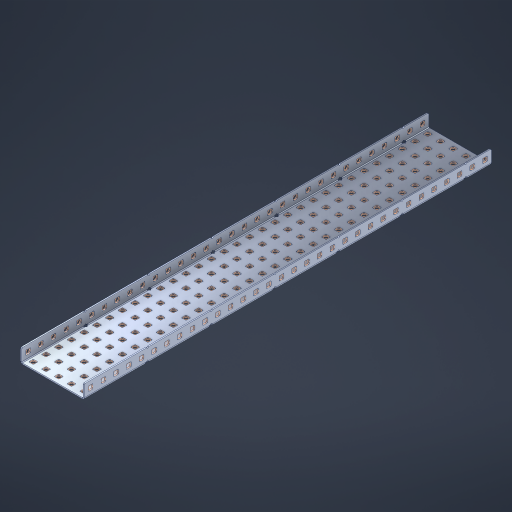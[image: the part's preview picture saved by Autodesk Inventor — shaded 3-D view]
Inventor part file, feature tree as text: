
AUTODESK INVENTOR PART (.ipt)
format: ipt  version: 2023 (Build 270158000, 158)  size: 2,352,640 bytes
history: native  units: in
note: dims shown in document units (in); Inventor stores cm internally (conversion verified against a paired STEP export)
features: other x229, extrude x223, sheet_metal_op x10, sketch x8, mirror x1, pattern_linear x1, chamfer x1
ambient origin geometry x8: Origin, YZ Plane, XZ Plane, XY Plane, X Axis, Y Axis, Z Axis, Center Point
bodies: Solid1 (feature_tree), Body (feature_tree)
feature tree (473):
  other  "Flange Pattern Plane"
  sheet_metal_op  "Flange Pattern"
  sheet_metal_op  "Body Pattern"
  other  "Arc Length"
  mirror  "Notch Mirror"
  pattern_linear  "Notch Pattern"  Spacing1=0.1875in  [1 undecoded]
  chamfer  "End Chamfer"
  extrude  "Half Cut"  Depth=0.0469in
  sketch  "Sketch1"  dims[d0=2.5in]
  other  "Plate1"
  sketch  "Sketch2"  dims[d1=16.0in]
  other  "Plate2"
  sheet_metal_op  "Bend1"
  sheet_metal_op  "Corner1"
  sketch  "Sketch3"  dims[d2=0.0469in]
  other  "Flange Pattern Sketch"
  sketch  "Sketch7"  dims[d3=0.0469in]
  other  "Srf1"
  other  "Srf2"
  sketch  "Sketch8"  dims[d4=0.0234in]
  sketch  "Sketch9"  dims[d5=0.0938in]
  other  "Srf91"
  sheet_metal_op  "Body Pattern Sketch"
  other  "Srf92"
  sketch  "Sketch13"  dims[d6=0.0469in]
  sketch  "Sketch14"  dims[d7=0.5in d8=90.0deg d9=0.0312in d10=0.1875in d11=0.0469in d12=0.0469in d16=0.182in d17=0.02in d18=0.0469in d19=0.0in d20=0.25in d21=0.25in d46=0.172in d47=1.0in d48=0.0in d49=0.182in d50=0.02in d51=0.25in d52=0.25in d53=0.0469in d54=0.0in d55=0.172in d56=1.0in d57=0.0in d60=12.5984in d62=0.5in d63=1.9685in d65=0.5in d85=0.1227in d86=0.1659in d88=0.04in d89=0.0469in d90=0.0in d91=0.04in d92=0.0491in d95=2.5in d96=0.04in d97=0.25in d98=45.0deg d101=0.0in d102=2.497in d131=2.5in d132=12.5984in d134=0.5in d139=0.5in]
  other  "Srf856"
  other  "Srf1310"
  other  "Srf1311"
  other  "Srf1312"
  other  "Srf1376"
  other  "Srf1377"
  other  "Srf1728"
  other  "Srf1755"
  other  "Srf1878"
  other  "Srf1879"
  other  "Srf1880"
  other  "Srf1881"
  other  "Srf1882"
  other  "Srf1883"
  other  "Srf1884"
  other  "Srf1885"
  other  "Srf1886"
  other  "Srf1887"
  other  "Srf1888"
  other  "Srf1889"
  other  "Srf1890"
  other  "Srf1891"
  other  "Srf1892"
  other  "Srf1893"
  other  "Srf1894"
  other  "Srf1895"
  other  "Srf1896"
  other  "Srf1897"
  other  "Srf1898"
  other  "Srf1899"
  other  "Srf1900"
  other  "Srf1901"
  other  "Srf1902"
  other  "Srf1903"
  other  "Srf1904"
  other  "Srf1905"
  other  "Srf1906"
  other  "Srf1942"
  other  "Srf1943"
  other  "Srf1944"
  other  "Srf1945"
  other  "Srf1946"
  other  "Srf1947"
  other  "Srf1948"
  other  "Srf1949"
  other  "Srf1950"
  other  "Srf1951"
  other  "Srf1952"
  other  "Srf1953"
  other  "Srf1954"
  other  "Srf1955"
  other  "Srf1956"
  other  "Srf1957"
  other  "Srf1958"
  other  "Srf1959"
  other  "Srf1960"
  other  "Srf1961"
  other  "Srf1962"
  other  "Srf1963"
  other  "Srf1964"
  other  "Srf1965"
  other  "Srf1966"
  other  "Srf1967"
  other  "Srf1968"
  other  "Srf1969"
  other  "Srf1970"
  other  "Srf2111"
  other  "Srf2112"
  other  "Srf2113"
  other  "Srf2114"
  other  "Srf2115"
  other  "Srf2116"
  other  "Srf2117"
  other  "Srf2118"
  other  "Srf2119"
  other  "Srf2120"
  other  "Srf2121"
  other  "Srf2122"
  other  "Srf2123"
  other  "Srf2124"
  other  "Srf2125"
  other  "Srf2126"
  other  "Srf2127"
  other  "Srf2128"
  other  "Srf2129"
  other  "Srf2130"
  other  "Srf2131"
  other  "Srf2132"
  other  "Srf2133"
  other  "Srf2134"
  other  "Srf2135"
  other  "Srf2136"
  other  "Srf2137"
  other  "Srf2138"
  other  "Srf2139"
  other  "Srf2146"
  other  "Srf2147"
  other  "Srf2148"
  other  "Srf2149"
  other  "Srf2150"
  other  "Srf2151"
  other  "Srf2152"
  other  "Srf2153"
  other  "Srf2154"
  other  "Srf2155"
  other  "Srf2156"
  other  "Srf2157"
  other  "Srf2158"
  other  "Srf2159"
  other  "Srf2160"
  other  "Srf2161"
  other  "Srf2162"
  other  "Srf2163"
  other  "Srf2164"
  other  "Srf2165"
  other  "Srf2166"
  other  "Srf2167"
  other  "Srf2168"
  other  "Srf2169"
  other  "Srf2170"
  other  "Srf2171"
  other  "Srf2172"
  other  "Srf2173"
  other  "Srf2174"
  other  "Srf2175"
  other  "Srf2176"
  other  "Srf2177"
  other  "Srf2178"
  other  "Srf2179"
  other  "Srf2180"
  other  "Srf2181"
  other  "Srf2182"
  other  "Srf2183"
  other  "Srf2184"
  other  "Srf2185"
  other  "Srf2186"
  other  "Srf2187"
  other  "Srf2188"
  other  "Srf2189"
  other  "Srf2190"
  other  "Srf2191"
  other  "Srf2192"
  other  "Srf2193"
  other  "Srf2194"
  other  "Srf2195"
  other  "Srf2196"
  other  "Srf2197"
  other  "Srf2198"
  other  "Srf2199"
  other  "Srf2200"
  other  "Srf2201"
  other  "Srf2202"
  other  "Srf2203"
  other  "Srf2204"
  other  "Srf2205"
  other  "Srf2206"
  other  "Srf2207"
  other  "Srf2208"
  other  "Srf2209"
  other  "Srf2210"
  other  "Srf2211"
  other  "Srf2212"
  other  "Srf2213"
  other  "Srf2214"
  other  "Srf2215"
  other  "Srf2216"
  other  "Srf2217"
  other  "Srf2218"
  other  "Srf2219"
  other  "Srf2220"
  other  "Srf2221"
  other  "Srf2222"
  other  "Srf2223"
  other  "Srf2224"
  other  "Srf2225"
  other  "Srf2226"
  other  "Srf2227"
  other  "Srf2228"
  other  "Srf2229"
  other  "Srf2230"
  other  "Srf2231"
  other  "Srf2232"
  other  "Srf2233"
  other  "Srf2234"
  other  "Srf2235"
  other  "Srf2236"
  other  "Srf2237"
  other  "Srf2238"
  other  "Srf2239"
  other  "Srf2240"
  other  "Srf2241"
  other  "Srf2242"
  other  "Srf2243"
  other  "Srf2244"
  other  "Srf2245"
  other  "Srf2246"
  other  "Srf2247"
  other  "Srf2248"
  other  "Srf2249"
  other  "Srf2250"
  other  "Srf2251"
  other  "Srf2252"
  other  "Srf2253"
  other  "Srf2254"
  other  "Srf2255"
  other  "Srf2256"
  other  "Srf2257"
  other  "Srf2258"
  other  "Srf2259"
  other  "Srf2260"
  other  "Srf2261"
  other  "Srf2262"
  other  "Srf2263"
  other  "Srf2264"
  other  "Srf2265"
  other  "Srf2266"
  other  "Srf2267"
  other  "Srf2268"
  other  "Srf2269"
  other  "Srf2270"
  sheet_metal_op  "Flange Stamp"
  sheet_metal_op  "Flange Circle"
  sheet_metal_op  "Body Stamp"
  sheet_metal_op  "Body Circle"
  sheet_metal_op  "Notch"
  extrude  "ExtrusionSrf2"  Depth=0.0469in
  extrude  "ExtrusionSrf92"  Depth=2.5in
  extrude  "ExtrusionSrf856"  Depth=0.02in
  extrude  "ExtrusionSrf1310"  Depth=0.0469in
  extrude  "ExtrusionSrf1311"  TaperAngle=0.0deg  [1 undecoded]
  extrude  "ExtrusionSrf1312"  Depth=0.25in
  extrude  "ExtrusionSrf1376"  Depth=0.25in
  extrude  "ExtrusionSrf1377"  Depth=2.5in
  extrude  "ExtrusionSrf1728"  Depth=2.5in TaperAngle=0.0deg
  extrude  "ExtrusionSrf1755"  Depth=2.5in
  extrude  "ExtrusionSrf1878"  Depth=0.02in
  extrude  "ExtrusionSrf1879"  Depth=0.25in
  extrude  "ExtrusionSrf1880"  Depth=0.25in
  extrude  "ExtrusionSrf1881"  Depth=0.0469in
  extrude  "ExtrusionSrf1882"  TaperAngle=0.0deg  [1 undecoded]
  extrude  "ExtrusionSrf1883"  Depth=2.5in
  extrude  "ExtrusionSrf1884"  Depth=2.5in TaperAngle=0.0deg
  extrude  "ExtrusionSrf1885"  Depth=2.5in
  extrude  "ExtrusionSrf1886"  Depth=2.5in
  extrude  "ExtrusionSrf1887"  Depth=2.5in
  extrude  "ExtrusionSrf1888"  Depth=2.5in
  extrude  "ExtrusionSrf1889"  Depth=2.5in
  extrude  "ExtrusionSrf1890"  Depth=0.0469in
  extrude  "ExtrusionSrf1891"  TaperAngle=0.0deg  [1 undecoded]
  extrude  "ExtrusionSrf1892"  Depth=2.5in
  extrude  "ExtrusionSrf1893"  Depth=2.5in
  extrude  "ExtrusionSrf1894"  Depth=2.5in
  extrude  "ExtrusionSrf1895"  Depth=0.25in TaperAngle=45.0deg
  extrude  "ExtrusionSrf1896"  TaperAngle=0.0deg  [1 undecoded]
  extrude  "ExtrusionSrf1897"  Depth=2.5in
  extrude  "ExtrusionSrf1898"  Depth=2.5in
  extrude  "ExtrusionSrf1899"  Depth=2.5in
  extrude  "ExtrusionSrf1900"  Depth=2.5in
  extrude  "ExtrusionSrf1901"  Depth=2.5in
  extrude  "ExtrusionSrf1902"  [1 undecoded]
  extrude  "ExtrusionSrf1903"  [1 undecoded]
  extrude  "ExtrusionSrf1904"  [1 undecoded]
  extrude  "ExtrusionSrf1905"  [1 undecoded]
  extrude  "ExtrusionSrf1906"  [1 undecoded]
  extrude  "ExtrusionSrf1942"  [1 undecoded]
  extrude  "ExtrusionSrf1943"  [1 undecoded]
  extrude  "ExtrusionSrf1944"  [1 undecoded]
  extrude  "ExtrusionSrf1945"  [1 undecoded]
  extrude  "ExtrusionSrf1946"  [1 undecoded]
  extrude  "ExtrusionSrf1947"  [1 undecoded]
  extrude  "ExtrusionSrf1948"  [1 undecoded]
  extrude  "ExtrusionSrf1949"  [1 undecoded]
  extrude  "ExtrusionSrf1950"  [1 undecoded]
  extrude  "ExtrusionSrf1951"  [1 undecoded]
  extrude  "ExtrusionSrf1952"  [1 undecoded]
  extrude  "ExtrusionSrf1953"  [1 undecoded]
  extrude  "ExtrusionSrf1954"  [1 undecoded]
  extrude  "ExtrusionSrf1955"  [1 undecoded]
  extrude  "ExtrusionSrf1956"  [1 undecoded]
  extrude  "ExtrusionSrf1957"  [1 undecoded]
  extrude  "ExtrusionSrf1958"  [1 undecoded]
  extrude  "ExtrusionSrf1959"  [1 undecoded]
  extrude  "ExtrusionSrf1960"  [1 undecoded]
  extrude  "ExtrusionSrf1961"  [1 undecoded]
  extrude  "ExtrusionSrf1962"  [1 undecoded]
  extrude  "ExtrusionSrf1963"  [1 undecoded]
  extrude  "ExtrusionSrf1964"  [1 undecoded]
  extrude  "ExtrusionSrf1965"  [1 undecoded]
  extrude  "ExtrusionSrf1966"  [1 undecoded]
  extrude  "ExtrusionSrf1967"  [1 undecoded]
  extrude  "ExtrusionSrf1968"  [1 undecoded]
  extrude  "ExtrusionSrf1969"  [1 undecoded]
  extrude  "ExtrusionSrf1970"  [1 undecoded]
  extrude  "ExtrusionSrf2111"  [1 undecoded]
  extrude  "ExtrusionSrf2112"  [1 undecoded]
  extrude  "ExtrusionSrf2113"  [1 undecoded]
  extrude  "ExtrusionSrf2114"  [1 undecoded]
  extrude  "ExtrusionSrf2115"  [1 undecoded]
  extrude  "ExtrusionSrf2116"  [1 undecoded]
  extrude  "ExtrusionSrf2117"  [1 undecoded]
  extrude  "ExtrusionSrf2118"  [1 undecoded]
  extrude  "ExtrusionSrf2119"  [1 undecoded]
  extrude  "ExtrusionSrf2120"  [1 undecoded]
  extrude  "ExtrusionSrf2121"  [1 undecoded]
  extrude  "ExtrusionSrf2122"  [1 undecoded]
  extrude  "ExtrusionSrf2123"  [1 undecoded]
  extrude  "ExtrusionSrf2124"  [1 undecoded]
  extrude  "ExtrusionSrf2125"  [1 undecoded]
  extrude  "ExtrusionSrf2126"  [1 undecoded]
  extrude  "ExtrusionSrf2127"  [1 undecoded]
  extrude  "ExtrusionSrf2128"  [1 undecoded]
  extrude  "ExtrusionSrf2129"  [1 undecoded]
  extrude  "ExtrusionSrf2130"  [1 undecoded]
  extrude  "ExtrusionSrf2131"  [1 undecoded]
  extrude  "ExtrusionSrf2132"  [1 undecoded]
  extrude  "ExtrusionSrf2133"  [1 undecoded]
  extrude  "ExtrusionSrf2134"  [1 undecoded]
  extrude  "ExtrusionSrf2135"  [1 undecoded]
  extrude  "ExtrusionSrf2136"  [1 undecoded]
  extrude  "ExtrusionSrf2137"  [1 undecoded]
  extrude  "ExtrusionSrf2138"  [1 undecoded]
  extrude  "ExtrusionSrf2139"  [1 undecoded]
  extrude  "ExtrusionSrf2146"  [1 undecoded]
  extrude  "ExtrusionSrf2147"  [1 undecoded]
  extrude  "ExtrusionSrf2148"  [1 undecoded]
  extrude  "ExtrusionSrf2149"  [1 undecoded]
  extrude  "ExtrusionSrf2150"  [1 undecoded]
  extrude  "ExtrusionSrf2151"  [1 undecoded]
  extrude  "ExtrusionSrf2152"  [1 undecoded]
  extrude  "ExtrusionSrf2153"  [1 undecoded]
  extrude  "ExtrusionSrf2154"  [1 undecoded]
  extrude  "ExtrusionSrf2155"  [1 undecoded]
  extrude  "ExtrusionSrf2156"  [1 undecoded]
  extrude  "ExtrusionSrf2157"  [1 undecoded]
  extrude  "ExtrusionSrf2158"  [1 undecoded]
  extrude  "ExtrusionSrf2159"  [1 undecoded]
  extrude  "ExtrusionSrf2160"  [1 undecoded]
  extrude  "ExtrusionSrf2161"  [1 undecoded]
  extrude  "ExtrusionSrf2162"  [1 undecoded]
  extrude  "ExtrusionSrf2163"  [1 undecoded]
  extrude  "ExtrusionSrf2164"  [1 undecoded]
  extrude  "ExtrusionSrf2165"  [1 undecoded]
  extrude  "ExtrusionSrf2166"  [1 undecoded]
  extrude  "ExtrusionSrf2167"  [1 undecoded]
  extrude  "ExtrusionSrf2168"  [1 undecoded]
  extrude  "ExtrusionSrf2169"  [1 undecoded]
  extrude  "ExtrusionSrf2170"  [1 undecoded]
  extrude  "ExtrusionSrf2171"  [1 undecoded]
  extrude  "ExtrusionSrf2172"  [1 undecoded]
  extrude  "ExtrusionSrf2173"  [1 undecoded]
  extrude  "ExtrusionSrf2174"  [1 undecoded]
  extrude  "ExtrusionSrf2175"  [1 undecoded]
  extrude  "ExtrusionSrf2176"  [1 undecoded]
  extrude  "ExtrusionSrf2177"  [1 undecoded]
  extrude  "ExtrusionSrf2178"  [1 undecoded]
  extrude  "ExtrusionSrf2179"  [1 undecoded]
  extrude  "ExtrusionSrf2180"  [1 undecoded]
  extrude  "ExtrusionSrf2181"  [1 undecoded]
  extrude  "ExtrusionSrf2182"  [1 undecoded]
  extrude  "ExtrusionSrf2183"  [1 undecoded]
  extrude  "ExtrusionSrf2184"  [1 undecoded]
  extrude  "ExtrusionSrf2185"  [1 undecoded]
  extrude  "ExtrusionSrf2186"  [1 undecoded]
  extrude  "ExtrusionSrf2187"  [1 undecoded]
  extrude  "ExtrusionSrf2188"  [1 undecoded]
  extrude  "ExtrusionSrf2189"  [1 undecoded]
  extrude  "ExtrusionSrf2190"  [1 undecoded]
  extrude  "ExtrusionSrf2191"  [1 undecoded]
  extrude  "ExtrusionSrf2192"  [1 undecoded]
  extrude  "ExtrusionSrf2193"  [1 undecoded]
  extrude  "ExtrusionSrf2194"  [1 undecoded]
  extrude  "ExtrusionSrf2195"  [1 undecoded]
  extrude  "ExtrusionSrf2196"  [1 undecoded]
  extrude  "ExtrusionSrf2197"  [1 undecoded]
  extrude  "ExtrusionSrf2198"  [1 undecoded]
  extrude  "ExtrusionSrf2199"  [1 undecoded]
  extrude  "ExtrusionSrf2200"  [1 undecoded]
  extrude  "ExtrusionSrf2201"  [1 undecoded]
  extrude  "ExtrusionSrf2202"  [1 undecoded]
  extrude  "ExtrusionSrf2203"  [1 undecoded]
  extrude  "ExtrusionSrf2204"  [1 undecoded]
  extrude  "ExtrusionSrf2205"  [1 undecoded]
  extrude  "ExtrusionSrf2206"  [1 undecoded]
  extrude  "ExtrusionSrf2207"  [1 undecoded]
  extrude  "ExtrusionSrf2208"  [1 undecoded]
  extrude  "ExtrusionSrf2209"  [1 undecoded]
  extrude  "ExtrusionSrf2210"  [1 undecoded]
  extrude  "ExtrusionSrf2211"  [1 undecoded]
  extrude  "ExtrusionSrf2212"  [1 undecoded]
  extrude  "ExtrusionSrf2213"  [1 undecoded]
  extrude  "ExtrusionSrf2214"  [1 undecoded]
  extrude  "ExtrusionSrf2215"  [1 undecoded]
  extrude  "ExtrusionSrf2216"  [1 undecoded]
  extrude  "ExtrusionSrf2217"  [1 undecoded]
  extrude  "ExtrusionSrf2218"  [1 undecoded]
  extrude  "ExtrusionSrf2219"  [1 undecoded]
  extrude  "ExtrusionSrf2220"  [1 undecoded]
  extrude  "ExtrusionSrf2221"  [1 undecoded]
  extrude  "ExtrusionSrf2222"  [1 undecoded]
  extrude  "ExtrusionSrf2223"  [1 undecoded]
  extrude  "ExtrusionSrf2224"  [1 undecoded]
  extrude  "ExtrusionSrf2225"  [1 undecoded]
  extrude  "ExtrusionSrf2226"  [1 undecoded]
  extrude  "ExtrusionSrf2227"  [1 undecoded]
  extrude  "ExtrusionSrf2228"  [1 undecoded]
  extrude  "ExtrusionSrf2229"  [1 undecoded]
  extrude  "ExtrusionSrf2230"  [1 undecoded]
  extrude  "ExtrusionSrf2231"  [1 undecoded]
  extrude  "ExtrusionSrf2232"  [1 undecoded]
  extrude  "ExtrusionSrf2233"  [1 undecoded]
  extrude  "ExtrusionSrf2234"  [1 undecoded]
  extrude  "ExtrusionSrf2235"  [1 undecoded]
  extrude  "ExtrusionSrf2236"  [1 undecoded]
  extrude  "ExtrusionSrf2237"  [1 undecoded]
  extrude  "ExtrusionSrf2238"  [1 undecoded]
  extrude  "ExtrusionSrf2239"  [1 undecoded]
  extrude  "ExtrusionSrf2240"  [1 undecoded]
  extrude  "ExtrusionSrf2241"  [1 undecoded]
  extrude  "ExtrusionSrf2242"  [1 undecoded]
  extrude  "ExtrusionSrf2243"  [1 undecoded]
  extrude  "ExtrusionSrf2244"  [1 undecoded]
  extrude  "ExtrusionSrf2245"  [1 undecoded]
  extrude  "ExtrusionSrf2246"  [1 undecoded]
  extrude  "ExtrusionSrf2247"  [1 undecoded]
  extrude  "ExtrusionSrf2248"  [1 undecoded]
  extrude  "ExtrusionSrf2249"  [1 undecoded]
  extrude  "ExtrusionSrf2250"  [1 undecoded]
  extrude  "ExtrusionSrf2251"  [1 undecoded]
  extrude  "ExtrusionSrf2252"  [1 undecoded]
  extrude  "ExtrusionSrf2253"  [1 undecoded]
  extrude  "ExtrusionSrf2254"  [1 undecoded]
  extrude  "ExtrusionSrf2255"  [1 undecoded]
  extrude  "ExtrusionSrf2256"  [1 undecoded]
  extrude  "ExtrusionSrf2257"  [1 undecoded]
  extrude  "ExtrusionSrf2258"  [1 undecoded]
  extrude  "ExtrusionSrf2259"  [1 undecoded]
  extrude  "ExtrusionSrf2260"  [1 undecoded]
  extrude  "ExtrusionSrf2261"  [1 undecoded]
  extrude  "ExtrusionSrf2262"  [1 undecoded]
  extrude  "ExtrusionSrf2263"  [1 undecoded]
  extrude  "ExtrusionSrf2264"  [1 undecoded]
  extrude  "ExtrusionSrf2265"  [1 undecoded]
  extrude  "ExtrusionSrf2266"  [1 undecoded]
  extrude  "ExtrusionSrf2267"  [1 undecoded]
  extrude  "ExtrusionSrf2268"  [1 undecoded]
  extrude  "ExtrusionSrf2269"  [1 undecoded]
  extrude  "ExtrusionSrf2270"  [1 undecoded]
note: 193 required parameter values undecoded (feature->parameter linkage not recoverable at this tier; creation-order binding heuristic only, values carry confidence <= 0.55)
